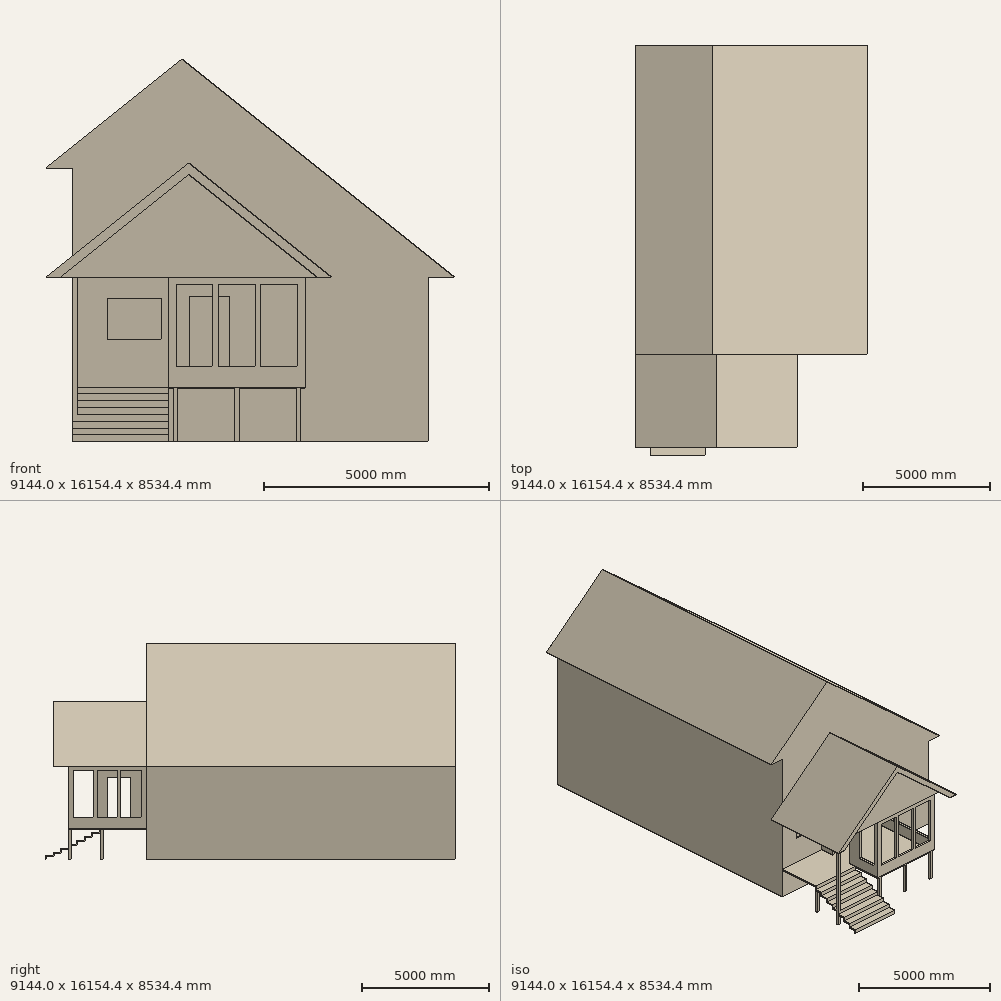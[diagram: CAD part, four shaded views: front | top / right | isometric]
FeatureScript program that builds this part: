
annotation { "Feature Type Name" : "Feature", "Feature Type Description" : "" }
export const myFeature = defineFeature(function(context is Context, id is Id, definition is map)
    precondition{}
    {
        {
            var Q0;
            Q0=qCreatedBy(makeId("Front.planeOp"),FACE);
            var sketch = newSketch(context, id + "F0", { "sketchPlane" : qUnion([Q0])});
            skLineSegment(sketch, "E0.bottom", {"start": v(0, 0) * mm, "end": v(-7924.8, 0) * mm});
            skLineSegment(sketch, "E1", {"start": v(-8534.4, 6096) * mm, "end": v(-7924.8, 6096) * mm});
            skLineSegment(sketch, "E2", {"start": v(0, 3657.6) * mm, "end": v(609.6, 3657.6) * mm});
            skLineSegment(sketch, "E3", {"start": v(-8534.4, 6096) * mm, "end": v(-5486.4, 8534.4) * mm});
            skLineSegment(sketch, "E4", {"start": v(0, 0) * mm, "end": v(0, 3657.6) * mm});
            skLineSegment(sketch, "E5", {"start": v(-7924.8, 0) * mm, "end": v(-7924.8, 6096) * mm});
            skLineSegment(sketch, "E6", {"start": v(-8534.4, 6096) * mm, "end": v(-2438.4, 6096) * mm, "construction": true});
            skLineSegment(sketch, "E7", {"start": v(-5486.4, 8534.4) * mm, "end": v(-2438.4, 6096) * mm});
            skLineSegment(sketch, "E8", {"start": v(-2438.4, 6096) * mm, "end": v(609.6, 3657.6) * mm});
            skSolve(sketch);
        }
        {
            var Q0;
            Q0=makeQuery(id+"F0.imprint","IMPRINT",FACE,{"disambiguationData":[TD([[makeQuery(id+"F0.imprint","IMPRINT",EDGE,{"derivedFrom":sQuery(id+"F0.wireOp",EDGE,"E0.bottom")}),-1.0]])]});
            extrude(context, id + "F1", {"entities" : qUnion([Q0]), "depth" : 12192 * mm, "offsetDistance" : 30.48 * mm});
        }
        {
            var Q0;
            Q0=makeQuery(id+"F1.opExtrude","CAP_FACE",FACE,{"disambiguationData":[OSD([sQuery(id+"F0.wireOp",EDGE,"E0.bottom"),sQuery(id+"F0.wireOp",EDGE,"E1"),sQuery(id+"F0.wireOp",EDGE,"E2"),sQuery(id+"F0.wireOp",EDGE,"E3"),sQuery(id+"F0.wireOp",EDGE,"IzW1YhJm-Oqc0-RvsV-s3cz-nyWO0slT3fW2"),sQuery(id+"F0.wireOp",EDGE,"E4"),sQuery(id+"F0.wireOp",EDGE,"E5")])],"isStart":false});
            var sketch = newSketch(context, id + "F2", { "sketchPlane" : qUnion([Q0])});
            skLineSegment(sketch, "E9", {"start": v(-7924.8, 1219.2) * mm, "end": v(0, 1219.2) * mm, "construction": true});
            skLineSegment(sketch, "E10.bottom", {"start": v(-7162.8, 3200.4) * mm, "end": v(-5943.6, 3200.4) * mm});
            skLineSegment(sketch, "E10.top", {"start": v(-7162.8, 2286) * mm, "end": v(-5943.6, 2286) * mm});
            skLineSegment(sketch, "E10.left", {"start": v(-7162.8, 3200.4) * mm, "end": v(-7162.8, 2286) * mm});
            skLineSegment(sketch, "E10.right", {"start": v(-5943.6, 3200.4) * mm, "end": v(-5943.6, 2286) * mm});
            skLineSegment(sketch, "E11.bottom", {"start": v(-5334, 1219.2) * mm, "end": v(-4419.6, 1219.2) * mm});
            skLineSegment(sketch, "E11.top", {"start": v(-5334, 3251.2) * mm, "end": v(-4419.6, 3251.2) * mm});
            skLineSegment(sketch, "E11.left", {"start": v(-5334, 1219.2) * mm, "end": v(-5334, 3251.2) * mm});
            skLineSegment(sketch, "E11.right", {"start": v(-4419.6, 1219.2) * mm, "end": v(-4419.6, 3251.2) * mm});
            skLineSegment(sketch, "E12", {"start": v(-8534.4, 3657.6) * mm, "end": v(-5334, 6217.92) * mm});
            skLineSegment(sketch, "E13", {"start": v(-5334, 6217.92) * mm, "end": v(-2133.6, 3657.6) * mm});
            skLineSegment(sketch, "E14", {"start": v(-2133.6, 3657.6) * mm, "end": v(-8534.4, 3657.6) * mm});
            skLineSegment(sketch, "E15.0", {"start": v(-5334, 5957.7) * mm, "end": v(-2712.88, 3860.8) * mm});
            skLineSegment(sketch, "E15.1", {"start": v(-7955.12, 3860.8) * mm, "end": v(-5334, 5957.7) * mm});
            skLineSegment(sketch, "E15.2", {"start": v(-2712.88, 3860.8) * mm, "end": v(-7955.12, 3860.8) * mm});
            skLineSegment(sketch, "E16", {"start": v(-7955.12, 3860.8) * mm, "end": v(-8209.12, 3657.6) * mm});
            skLineSegment(sketch, "E17", {"start": v(-2712.88, 3860.8) * mm, "end": v(-2458.88, 3657.6) * mm});
            skSolve(sketch);
        }
        {
            var Q0;
            Q0=makeQuery(id+"F1.opExtrude","SWEPT_FACE",FACE,{"disambiguationData":[OSD([sQuery(id+"F0.wireOp",EDGE,"E5")])]});
            var sketch = newSketch(context, id + "F3", { "sketchPlane" : qUnion([Q0])});
            skLineSegment(sketch, "E18", {"start": v(14020.8, 1219.2) * mm, "end": v(14020.8, 1066.8) * mm});
            skLineSegment(sketch, "E19", {"start": v(14020.8, 1066.8) * mm, "end": v(14325.6, 1066.8) * mm});
            skLineSegment(sketch, "E20", {"start": v(14325.6, 1066.8) * mm, "end": v(14325.6, 914.4) * mm});
            skLineSegment(sketch, "E21", {"start": v(14325.6, 914.4) * mm, "end": v(14630.4, 914.4) * mm});
            skLineSegment(sketch, "E22", {"start": v(14630.4, 914.4) * mm, "end": v(14630.4, 762) * mm});
            skLineSegment(sketch, "E23", {"start": v(14630.4, 762) * mm, "end": v(14935.2, 762) * mm});
            skLineSegment(sketch, "E24", {"start": v(14935.2, 762) * mm, "end": v(14935.2, 609.6) * mm});
            skLineSegment(sketch, "E25", {"start": v(14935.2, 609.6) * mm, "end": v(15240, 609.6) * mm});
            skLineSegment(sketch, "E26", {"start": v(15240, 609.6) * mm, "end": v(15240, 457.2) * mm});
            skLineSegment(sketch, "E27", {"start": v(15240, 457.2) * mm, "end": v(15544.8, 457.2) * mm});
            skLineSegment(sketch, "E28", {"start": v(15544.8, 457.2) * mm, "end": v(15544.8, 304.8) * mm});
            skLineSegment(sketch, "E29", {"start": v(15544.8, 304.8) * mm, "end": v(15849.6, 304.8) * mm});
            skLineSegment(sketch, "E30", {"start": v(15849.6, 304.8) * mm, "end": v(15849.6, 152.4) * mm});
            skLineSegment(sketch, "E31", {"start": v(15849.6, 152.4) * mm, "end": v(16154.4, 152.4) * mm});
            skLineSegment(sketch, "E32", {"start": v(16154.4, 152.4) * mm, "end": v(16154.4, 0) * mm});
            skLineSegment(sketch, "E33", {"start": v(14020.8, 1219.2) * mm, "end": v(12192, 1219.2) * mm});
            skLineSegment(sketch, "E34", {"start": v(16154.4, 0) * mm, "end": v(12192, 0) * mm});
            skLineSegment(sketch, "E35.0", {"start": v(13982.7, 1181.1) * mm, "end": v(12192, 1181.1) * mm});
            skLineSegment(sketch, "E35.1", {"start": v(13982.7, 1181.1) * mm, "end": v(13982.7, 1028.7) * mm});
            skLineSegment(sketch, "E35.2", {"start": v(13982.7, 1028.7) * mm, "end": v(14287.5, 1028.7) * mm});
            skLineSegment(sketch, "E35.3", {"start": v(14287.5, 1028.7) * mm, "end": v(14287.5, 876.3) * mm});
            skLineSegment(sketch, "E35.4", {"start": v(14287.5, 876.3) * mm, "end": v(14592.3, 876.3) * mm});
            skLineSegment(sketch, "E35.5", {"start": v(14592.3, 876.3) * mm, "end": v(14592.3, 723.9) * mm});
            skLineSegment(sketch, "E35.6", {"start": v(15506.7, 266.7) * mm, "end": v(15811.5, 266.7) * mm});
            skLineSegment(sketch, "E35.7", {"start": v(15811.5, 266.7) * mm, "end": v(15811.5, 114.3) * mm});
            skLineSegment(sketch, "E35.8", {"start": v(15811.5, 114.3) * mm, "end": v(16116.3, 114.3) * mm});
            skLineSegment(sketch, "E35.9", {"start": v(16116.3, 114.3) * mm, "end": v(16116.3, 0) * mm});
            skLineSegment(sketch, "E35.10", {"start": v(15506.7, 419.1) * mm, "end": v(15506.7, 266.7) * mm});
            skLineSegment(sketch, "E35.11", {"start": v(15201.9, 419.1) * mm, "end": v(15506.7, 419.1) * mm});
            skLineSegment(sketch, "E35.12", {"start": v(15201.9, 571.5) * mm, "end": v(15201.9, 419.1) * mm});
            skLineSegment(sketch, "E35.13", {"start": v(14897.1, 571.5) * mm, "end": v(15201.9, 571.5) * mm});
            skLineSegment(sketch, "E35.14", {"start": v(14897.1, 723.9) * mm, "end": v(14897.1, 571.5) * mm});
            skLineSegment(sketch, "E35.15", {"start": v(14592.3, 723.9) * mm, "end": v(14897.1, 723.9) * mm});
            skSolve(sketch);
        }
        {
            var Q0;
            Q0=makeQuery(id+"F3.imprint","IMPRINT",FACE,{"disambiguationData":[TD([[makeQuery(id+"F3.imprint","IMPRINT",EDGE,{"derivedFrom":sQuery(id+"F3.wireOp",EDGE,"E18")}),-1.0]])]});
            extrude(context, id + "F4", {"entities" : qUnion([Q0]), "oppositeDirection" : true, "depth" : 2133.6 * mm, "offsetDistance" : 30.48 * mm});
        }
        {
            var Q0;
            Q0=makeQuery(id+"F2.imprint","IMPRINT",FACE,{"disambiguationData":[TD([[makeQuery(id+"F2.imprint","IMPRINT",EDGE,{"derivedFrom":sQuery(id+"F2.wireOp",EDGE,"E10.bottom")}),-1.0]])]});
            var Q1;
            Q1=makeQuery(id+"F2.imprint","IMPRINT",FACE,{"disambiguationData":[TD([[makeQuery(id+"F2.imprint","IMPRINT",EDGE,{"derivedFrom":sQuery(id+"F2.wireOp",EDGE,"E11.bottom")}),1.0]])]});
            var Q2;
            {var subQ0=sQuery(id+"F2.wireOp",EDGE,"E14");var subQ1=sQuery(id+"F2.wireOp",EDGE,"E12");var subQ2=makeQuery(id+"F2.imprint","INTERSECT",VERTEX,{"derivedFrom":[subQ1,subQ0]});Q2=makeQuery(id+"F2.imprint","IMPRINT",FACE,{"disambiguationData":[TD([[makeQuery(id+"F2.imprint","IMPRINT",EDGE,{"disambiguationData":[TD([[subQ2,-1.0]])],"derivedFrom":subQ1}),-1.0]])]});}
            extrude(context, id + "F5", {"entities" : qUnion([Q0, Q1, Q2]), "operationType" : NewBodyOperationType.REMOVE, "oppositeDirection" : true, "depth" : 30.48 * mm, "offsetDistance" : 30.48 * mm});
        }
        {
            var Q0;
            Q0=makeQuery(id+"F4.opExtrude","CAP_FACE",FACE,{"disambiguationData":[OSD([sQuery(id+"F0.wireOp",EDGE,"E5"),sQuery(id+"F3.wireOp",EDGE,"E18"),sQuery(id+"F3.wireOp",EDGE,"E19"),sQuery(id+"F3.wireOp",EDGE,"E20"),sQuery(id+"F3.wireOp",EDGE,"E21"),sQuery(id+"F3.wireOp",EDGE,"E22"),sQuery(id+"F3.wireOp",EDGE,"E23"),sQuery(id+"F3.wireOp",EDGE,"E24"),sQuery(id+"F3.wireOp",EDGE,"E25"),sQuery(id+"F3.wireOp",EDGE,"E26"),sQuery(id+"F3.wireOp",EDGE,"E27"),sQuery(id+"F3.wireOp",EDGE,"E28"),sQuery(id+"F3.wireOp",EDGE,"E29"),sQuery(id+"F3.wireOp",EDGE,"E30"),sQuery(id+"F3.wireOp",EDGE,"E31"),sQuery(id+"F3.wireOp",EDGE,"E32"),sQuery(id+"F3.wireOp",EDGE,"E33"),sQuery(id+"F3.wireOp",EDGE,"E34")])],"isStart":false});
            var sketch = newSketch(context, id + "F6", { "sketchPlane" : qUnion([Q0])});
            skLineSegment(sketch, "E36", {"start": v(-12192, 1219.2) * mm, "end": v(-15240, 1219.2) * mm});
            skLineSegment(sketch, "E37", {"start": v(-15240, 1219.2) * mm, "end": v(-15240, 1181.1) * mm});
            skLineSegment(sketch, "E38", {"start": v(-15240, 1181.1) * mm, "end": v(-12192, 1181.1) * mm});
            skLineSegment(sketch, "E39", {"start": v(-12192, 1181.1) * mm, "end": v(-12192, 1219.2) * mm});
            skSolve(sketch);
        }
        {
            var Q0;
            {var subQ3=sQuery(id+"F6.wireOp",EDGE,"E37");Q0=makeQuery(id+"F6.imprint","IMPRINT",FACE,{"disambiguationData":[TD([[makeQuery(id+"F6.imprint","IMPRINT",EDGE,{"derivedFrom":subQ3}),1.0]])]});}
            var Q1;
            {var subQ3=sQuery(id+"F6.wireOp",EDGE,"E39");Q1=makeQuery(id+"F6.imprint","IMPRINT",FACE,{"disambiguationData":[TD([[makeQuery(id+"F6.imprint","IMPRINT",EDGE,{"derivedFrom":subQ3}),1.0]])]});}
            extrude(context, id + "F7", {"entities" : qUnion([Q0, Q1]), "depth" : 3048 * mm, "offsetDistance" : 30.48 * mm});
        }
        {
            var Q0;
            Q0=makeQuery(id+"F7.opExtrude","SWEPT_FACE",FACE,{"disambiguationData":[OSD([sQuery(id+"F6.wireOp",EDGE,"E38")])]});
            var sketch = newSketch(context, id + "F8", { "sketchPlane" : qUnion([Q0])});
            skLineSegment(sketch, "E40.bottom", {"start": v(-5689.6, 15240) * mm, "end": v(-5588, 15240) * mm});
            skLineSegment(sketch, "E40.top", {"start": v(-5689.6, 15138.4) * mm, "end": v(-5588, 15138.4) * mm});
            skLineSegment(sketch, "E40.left", {"start": v(-5689.6, 15240) * mm, "end": v(-5689.6, 15138.4) * mm});
            skLineSegment(sketch, "E40.right", {"start": v(-5588, 15240) * mm, "end": v(-5588, 15138.4) * mm});
            skLineSegment(sketch, "E41.bottom", {"start": v(-2844.8, 15240) * mm, "end": v(-2946.4, 15240) * mm});
            skLineSegment(sketch, "E41.top", {"start": v(-2844.8, 15138.4) * mm, "end": v(-2946.4, 15138.4) * mm});
            skLineSegment(sketch, "E41.left", {"start": v(-2844.8, 15240) * mm, "end": v(-2844.8, 15138.4) * mm});
            skLineSegment(sketch, "E41.right", {"start": v(-2946.4, 15240) * mm, "end": v(-2946.4, 15138.4) * mm});
            skLineSegment(sketch, "E42.bottom", {"start": v(-4216.4, 15240) * mm, "end": v(-4318, 15240) * mm});
            skLineSegment(sketch, "E42.top", {"start": v(-4216.4, 15138.4) * mm, "end": v(-4318, 15138.4) * mm});
            skLineSegment(sketch, "E42.left", {"start": v(-4216.4, 15240) * mm, "end": v(-4216.4, 15138.4) * mm});
            skLineSegment(sketch, "E42.right", {"start": v(-4318, 15240) * mm, "end": v(-4318, 15138.4) * mm});
            skLineSegment(sketch, "E43.bottom", {"start": v(-7823.2, 13982.7) * mm, "end": v(-7721.6, 13982.7) * mm});
            skLineSegment(sketch, "E43.top", {"start": v(-7823.2, 13881.1) * mm, "end": v(-7721.6, 13881.1) * mm});
            skLineSegment(sketch, "E43.left", {"start": v(-7823.2, 13982.7) * mm, "end": v(-7823.2, 13881.1) * mm});
            skLineSegment(sketch, "E43.right", {"start": v(-7721.6, 13982.7) * mm, "end": v(-7721.6, 13881.1) * mm});
            skLineSegment(sketch, "E44.bottom", {"start": v(-5994.4, 13881.1) * mm, "end": v(-5892.8, 13881.1) * mm});
            skLineSegment(sketch, "E44.top", {"start": v(-5994.4, 13982.7) * mm, "end": v(-5892.8, 13982.7) * mm});
            skLineSegment(sketch, "E44.left", {"start": v(-5994.4, 13881.1) * mm, "end": v(-5994.4, 13982.7) * mm});
            skLineSegment(sketch, "E44.right", {"start": v(-5892.8, 13881.1) * mm, "end": v(-5892.8, 13982.7) * mm});
            skSolve(sketch);
        }
        {
            var Q0;
            Q0=makeQuery(id+"F8.imprint","IMPRINT",FACE,{"disambiguationData":[TD([[makeQuery(id+"F8.imprint","IMPRINT",EDGE,{"derivedFrom":sQuery(id+"F8.wireOp",EDGE,"E44.bottom")}),1.0]])]});
            var Q1;
            Q1=makeQuery(id+"F8.imprint","IMPRINT",FACE,{"disambiguationData":[TD([[makeQuery(id+"F8.imprint","IMPRINT",EDGE,{"derivedFrom":sQuery(id+"F8.wireOp",EDGE,"E40.bottom")}),-1.0]])]});
            var Q2;
            Q2=makeQuery(id+"F8.imprint","IMPRINT",FACE,{"disambiguationData":[TD([[makeQuery(id+"F8.imprint","IMPRINT",EDGE,{"derivedFrom":sQuery(id+"F8.wireOp",EDGE,"E42.bottom")}),1.0]])]});
            var Q3;
            Q3=makeQuery(id+"F8.imprint","IMPRINT",FACE,{"disambiguationData":[TD([[makeQuery(id+"F8.imprint","IMPRINT",EDGE,{"derivedFrom":sQuery(id+"F8.wireOp",EDGE,"E41.bottom")}),1.0]])]});
            var Q4;
            Q4=makeQuery(id+"F8.imprint","IMPRINT",FACE,{"disambiguationData":[TD([[makeQuery(id+"F8.imprint","IMPRINT",EDGE,{"derivedFrom":sQuery(id+"F8.wireOp",EDGE,"E43.bottom")}),-1.0]])]});
            var Q5;
            Q5=makeQuery(id+"F8.imprint","IMPRINT",FACE,{"disambiguationData":[TD([[makeQuery(id+"F8.imprint","IMPRINT",EDGE,{"derivedFrom":sQuery(id+"F8.wireOp",EDGE,"E40.bottom")}),1.0]])]});
            extrude(context, id + "F9", {"entities" : qUnion([Q0, Q1, Q2, Q3, Q4, Q5]), "depth" : 1181.1 * mm, "offsetDistance" : 30.48 * mm});
        }
        {
            var Q0;
            Q0=makeQuery(id+"F9.opExtrude","SWEPT_BODY",BODY,{"disambiguationData":[OSD([sQuery(id+"F8.wireOp",EDGE,"E41.bottom"),sQuery(id+"F8.wireOp",EDGE,"E41.top"),sQuery(id+"F8.wireOp",EDGE,"E41.left"),sQuery(id+"F8.wireOp",EDGE,"E41.right")])]});
            var Q1;
            Q1=makeQuery(id+"F9.opExtrude","SWEPT_BODY",BODY,{"disambiguationData":[OSD([sQuery(id+"F8.wireOp",EDGE,"E40.bottom"),sQuery(id+"F8.wireOp",EDGE,"E40.top"),sQuery(id+"F8.wireOp",EDGE,"E40.left"),sQuery(id+"F8.wireOp",EDGE,"E40.right")])]});
            var Q2;
            Q2=makeQuery(id+"F7.opExtrude","SWEPT_BODY",BODY,{"disambiguationData":[OSD([sQuery(id+"F6.wireOp",EDGE,"E36"),sQuery(id+"F6.wireOp",EDGE,"E37"),sQuery(id+"F6.wireOp",EDGE,"E38"),sQuery(id+"F6.wireOp",EDGE,"E39")])]});
            var Q3;
            Q3=makeQuery(id+"F4.opExtrude","SWEPT_BODY",BODY,{"disambiguationData":[OSD([sQuery(id+"F0.wireOp",EDGE,"E5"),sQuery(id+"F3.wireOp",EDGE,"E18"),sQuery(id+"F3.wireOp",EDGE,"E19"),sQuery(id+"F3.wireOp",EDGE,"E20"),sQuery(id+"F3.wireOp",EDGE,"E21"),sQuery(id+"F3.wireOp",EDGE,"E22"),sQuery(id+"F3.wireOp",EDGE,"E23"),sQuery(id+"F3.wireOp",EDGE,"E24"),sQuery(id+"F3.wireOp",EDGE,"E25"),sQuery(id+"F3.wireOp",EDGE,"E26"),sQuery(id+"F3.wireOp",EDGE,"E27"),sQuery(id+"F3.wireOp",EDGE,"E28"),sQuery(id+"F3.wireOp",EDGE,"E29"),sQuery(id+"F3.wireOp",EDGE,"E30"),sQuery(id+"F3.wireOp",EDGE,"E31"),sQuery(id+"F3.wireOp",EDGE,"E32"),sQuery(id+"F3.wireOp",EDGE,"E33"),sQuery(id+"F3.wireOp",EDGE,"E34"),sQuery(id+"F3.wireOp",EDGE,"E35.0"),sQuery(id+"F3.wireOp",EDGE,"E35.1"),sQuery(id+"F3.wireOp",EDGE,"E35.2"),sQuery(id+"F3.wireOp",EDGE,"E35.3"),sQuery(id+"F3.wireOp",EDGE,"E35.4"),sQuery(id+"F3.wireOp",EDGE,"E35.5"),sQuery(id+"F3.wireOp",EDGE,"E35.6"),sQuery(id+"F3.wireOp",EDGE,"E35.7"),sQuery(id+"F3.wireOp",EDGE,"E35.8"),sQuery(id+"F3.wireOp",EDGE,"E35.9"),sQuery(id+"F3.wireOp",EDGE,"E35.10"),sQuery(id+"F3.wireOp",EDGE,"E35.11"),sQuery(id+"F3.wireOp",EDGE,"E35.12"),sQuery(id+"F3.wireOp",EDGE,"E35.13"),sQuery(id+"F3.wireOp",EDGE,"E35.14"),sQuery(id+"F3.wireOp",EDGE,"E35.15")])]});
            var Q4;
            Q4=makeQuery(id+"F9.opExtrude","SWEPT_BODY",BODY,{"disambiguationData":[OSD([sQuery(id+"F8.wireOp",EDGE,"E44.bottom"),sQuery(id+"F8.wireOp",EDGE,"E44.top"),sQuery(id+"F8.wireOp",EDGE,"E44.left"),sQuery(id+"F8.wireOp",EDGE,"E44.right")])]});
            var Q5;
            Q5=makeQuery(id+"F9.opExtrude","SWEPT_BODY",BODY,{"disambiguationData":[OSD([sQuery(id+"F8.wireOp",EDGE,"E43.bottom"),sQuery(id+"F8.wireOp",EDGE,"E43.top"),sQuery(id+"F8.wireOp",EDGE,"E43.left"),sQuery(id+"F8.wireOp",EDGE,"E43.right")])]});
            var Q6;
            Q6=makeQuery(id+"F9.opExtrude","SWEPT_BODY",BODY,{"disambiguationData":[OSD([sQuery(id+"F8.wireOp",EDGE,"E42.bottom"),sQuery(id+"F8.wireOp",EDGE,"E42.top"),sQuery(id+"F8.wireOp",EDGE,"E42.left"),sQuery(id+"F8.wireOp",EDGE,"E42.right")])]});
            booleanBodies(context, id + "F10", {"operationType" : BooleanOperationType.UNION, "tools" : qUnion([Q0, Q1, Q2, Q3, Q4, Q5, Q6])});
        }
        {
            var Q0;
            Q0=makeQuery(id+"F10.opBoolean","MERGE",FACE,{"derivedFrom":[makeQuery(id+"F4.opExtrude","SWEPT_FACE",FACE,{"disambiguationData":[OSD([sQuery(id+"F3.wireOp",EDGE,"E33")])]}),makeQuery(id+"F7.opExtrude","SWEPT_FACE",FACE,{"disambiguationData":[OSD([sQuery(id+"F6.wireOp",EDGE,"E36")])]})]});
            var sketch = newSketch(context, id + "F11", { "sketchPlane" : qUnion([Q0])});
            skLineSegment(sketch, "E45.bottom", {"start": v(-5791.2, -15240) * mm, "end": v(-2743.2, -15240) * mm});
            skLineSegment(sketch, "E45.top", {"start": v(-5791.2, -12192) * mm, "end": v(-2743.2, -12192) * mm});
            skLineSegment(sketch, "E45.left", {"start": v(-5791.2, -15240) * mm, "end": v(-5791.2, -12192) * mm});
            skLineSegment(sketch, "E45.right", {"start": v(-2743.2, -15240) * mm, "end": v(-2743.2, -12192) * mm});
            skLineSegment(sketch, "E46.top", {"start": v(-2844.8, -15138.4) * mm, "end": v(-5689.6, -15138.4) * mm});
            skLineSegment(sketch, "E46.left", {"start": v(-2844.8, -12192) * mm, "end": v(-2844.8, -15138.4) * mm});
            skLineSegment(sketch, "E46.right", {"start": v(-5689.6, -12192) * mm, "end": v(-5689.6, -15138.4) * mm});
            skSolve(sketch);
        }
        {
            var Q0;
            {var subQ8=sQuery(id+"F11.wireOp",EDGE,"E45.bottom");Q0=makeQuery(id+"F11.imprint","IMPRINT",FACE,{"disambiguationData":[TD([[makeQuery(id+"F11.imprint","IMPRINT",EDGE,{"derivedFrom":subQ8}),-1.0]])]});}
            extrude(context, id + "F12", {"entities" : qUnion([Q0]), "depth" : 2438.4 * mm, "offsetDistance" : 30.48 * mm});
        }
        {
            var Q0;
            Q0=makeQuery(id+"F4.opExtrude","SWEPT_FACE",FACE,{"disambiguationData":[OSD([sQuery(id+"F3.wireOp",EDGE,"E25")])]});
            var sketch = newSketch(context, id + "F13", { "sketchPlane" : qUnion([Q0])});
            skLineSegment(sketch, "E47.bottom", {"start": v(-7924.8, -15240) * mm, "end": v(-7823.2, -15240) * mm});
            skLineSegment(sketch, "E47.top", {"start": v(-7924.8, -15138.4) * mm, "end": v(-7823.2, -15138.4) * mm});
            skLineSegment(sketch, "E47.left", {"start": v(-7924.8, -15240) * mm, "end": v(-7924.8, -15138.4) * mm});
            skLineSegment(sketch, "E47.right", {"start": v(-7823.2, -15240) * mm, "end": v(-7823.2, -15138.4) * mm});
            skSolve(sketch);
        }
        {
            var Q0;
            Q0=qSketchRegion(id+"F13",true);
            extrude(context, id + "F14", {"entities" : qUnion([Q0]), "operationType" : NewBodyOperationType.ADD, "depth" : 3048 * mm, "offsetDistance" : 30.48 * mm});
        }
        {
            var Q0;
            Q0=makeQuery(id+"F12.opExtrude","SWEPT_FACE",FACE,{"disambiguationData":[OSD([sQuery(id+"F11.wireOp",EDGE,"E45.bottom")])]});
            var sketch = newSketch(context, id + "F15", { "sketchPlane" : qUnion([Q0])});
            skLineSegment(sketch, "E48.bottom", {"start": v(-5613.4, 3505.2) * mm, "end": v(-4800.6, 3505.2) * mm});
            skLineSegment(sketch, "E48.top", {"start": v(-5613.4, 1676.4) * mm, "end": v(-4800.6, 1676.4) * mm});
            skLineSegment(sketch, "E48.left", {"start": v(-5613.4, 3505.2) * mm, "end": v(-5613.4, 1676.4) * mm});
            skLineSegment(sketch, "E48.right", {"start": v(-4800.6, 3505.2) * mm, "end": v(-4800.6, 1676.4) * mm});
            skLineSegment(sketch, "E49.bottom", {"start": v(-4673.6, 1676.4) * mm, "end": v(-3860.8, 1676.4) * mm});
            skLineSegment(sketch, "E49.top", {"start": v(-4673.6, 3505.2) * mm, "end": v(-3860.8, 3505.2) * mm});
            skLineSegment(sketch, "E49.left", {"start": v(-4673.6, 1676.4) * mm, "end": v(-4673.6, 3505.2) * mm});
            skLineSegment(sketch, "E49.right", {"start": v(-3860.8, 1676.4) * mm, "end": v(-3860.8, 3505.2) * mm});
            skLineSegment(sketch, "E50.bottom", {"start": v(-3733.8, 3505.2) * mm, "end": v(-2921, 3505.2) * mm});
            skLineSegment(sketch, "E50.top", {"start": v(-3733.8, 1676.4) * mm, "end": v(-2921, 1676.4) * mm});
            skLineSegment(sketch, "E50.left", {"start": v(-3733.8, 3505.2) * mm, "end": v(-3733.8, 1676.4) * mm});
            skLineSegment(sketch, "E50.right", {"start": v(-2921, 3505.2) * mm, "end": v(-2921, 1676.4) * mm});
            skSolve(sketch);
        }
        {
            var Q0;
            Q0=qSketchRegion(id+"F15",true);
            extrude(context, id + "F16", {"entities" : qUnion([Q0]), "operationType" : NewBodyOperationType.REMOVE, "oppositeDirection" : true, "depth" : 304.8 * mm, "offsetDistance" : 30.48 * mm});
        }
        {
            var Q0;
            Q0=makeQuery(id+"F12.opExtrude","SWEPT_FACE",FACE,{"disambiguationData":[OSD([sQuery(id+"F11.wireOp",EDGE,"E45.right")])]});
            var sketch = newSketch(context, id + "F17", { "sketchPlane" : qUnion([Q0])});
            skLineSegment(sketch, "E51.bottom", {"start": v(-15062.2, 3505.2) * mm, "end": v(-14249.4, 3505.2) * mm});
            skLineSegment(sketch, "E51.top", {"start": v(-15062.2, 1676.4) * mm, "end": v(-14249.4, 1676.4) * mm});
            skLineSegment(sketch, "E51.left", {"start": v(-15062.2, 3505.2) * mm, "end": v(-15062.2, 1676.4) * mm});
            skLineSegment(sketch, "E51.right", {"start": v(-14249.4, 3505.2) * mm, "end": v(-14249.4, 1676.4) * mm});
            skLineSegment(sketch, "E52.bottom", {"start": v(-14122.4, 1676.4) * mm, "end": v(-13309.6, 1676.4) * mm});
            skLineSegment(sketch, "E52.top", {"start": v(-14122.4, 3505.2) * mm, "end": v(-13309.6, 3505.2) * mm});
            skLineSegment(sketch, "E52.left", {"start": v(-14122.4, 1676.4) * mm, "end": v(-14122.4, 3505.2) * mm});
            skLineSegment(sketch, "E52.right", {"start": v(-13309.6, 1676.4) * mm, "end": v(-13309.6, 3505.2) * mm});
            skLineSegment(sketch, "E53.bottom", {"start": v(-13182.6, 3505.2) * mm, "end": v(-12369.8, 3505.2) * mm});
            skLineSegment(sketch, "E53.top", {"start": v(-13182.6, 1676.4) * mm, "end": v(-12369.8, 1676.4) * mm});
            skLineSegment(sketch, "E53.left", {"start": v(-13182.6, 3505.2) * mm, "end": v(-13182.6, 1676.4) * mm});
            skLineSegment(sketch, "E53.right", {"start": v(-12369.8, 3505.2) * mm, "end": v(-12369.8, 1676.4) * mm});
            skSolve(sketch);
        }
        {
            var Q0;
            Q0=qSketchRegion(id+"F17",true);
            extrude(context, id + "F18", {"entities" : qUnion([Q0]), "operationType" : NewBodyOperationType.REMOVE, "oppositeDirection" : true, "depth" : 304.8 * mm, "offsetDistance" : 30.48 * mm});
        }
        {
            var Q0;
            Q0=makeQuery(id+"F12.opExtrude","SWEPT_FACE",FACE,{"disambiguationData":[OSD([sQuery(id+"F11.wireOp",EDGE,"E45.left")])]});
            var sketch = newSketch(context, id + "F19", { "sketchPlane" : qUnion([Q0])});
            skLineSegment(sketch, "E54.bottom", {"start": v(12801.6, 1219.2) * mm, "end": v(13716, 1219.2) * mm});
            skLineSegment(sketch, "E54.top", {"start": v(12801.6, 3251.2) * mm, "end": v(13716, 3251.2) * mm});
            skLineSegment(sketch, "E54.left", {"start": v(12801.6, 1219.2) * mm, "end": v(12801.6, 3251.2) * mm});
            skLineSegment(sketch, "E54.right", {"start": v(13716, 1219.2) * mm, "end": v(13716, 3251.2) * mm});
            skLineSegment(sketch, "E55.bottom", {"start": v(14249.4, 3505.2) * mm, "end": v(15062.2, 3505.2) * mm});
            skLineSegment(sketch, "E55.top", {"start": v(14249.4, 1676.4) * mm, "end": v(15062.2, 1676.4) * mm});
            skLineSegment(sketch, "E55.left", {"start": v(14249.4, 3505.2) * mm, "end": v(14249.4, 1676.4) * mm});
            skLineSegment(sketch, "E55.right", {"start": v(15062.2, 3505.2) * mm, "end": v(15062.2, 1676.4) * mm});
            skSolve(sketch);
        }
        {
            var Q0;
            Q0=makeQuery(id+"F19.imprint","IMPRINT",FACE,{"disambiguationData":[TD([[makeQuery(id+"F19.imprint","IMPRINT",EDGE,{"derivedFrom":sQuery(id+"F19.wireOp",EDGE,"E54.bottom")}),-1.0]])]});
            var Q1;
            Q1=makeQuery(id+"F19.imprint","IMPRINT",FACE,{"disambiguationData":[TD([[makeQuery(id+"F19.imprint","IMPRINT",EDGE,{"derivedFrom":sQuery(id+"F19.wireOp",EDGE,"E55.bottom")}),-1.0]])]});
            extrude(context, id + "F20", {"entities" : qUnion([Q0, Q1]), "operationType" : NewBodyOperationType.REMOVE, "oppositeDirection" : true, "depth" : 304.8 * mm, "offsetDistance" : 30.48 * mm});
        }
        {
            var Q0;
            {var subQ0=sQuery(id+"F2.wireOp",EDGE,"E15.0");Q0=makeQuery(id+"F2.imprint","IMPRINT",FACE,{"disambiguationData":[TD([[makeQuery(id+"F2.imprint","IMPRINT",EDGE,{"derivedFrom":subQ0}),-1.0]])]});}
            var Q1;
            {var subQ0=sQuery(id+"F2.wireOp",EDGE,"E17");Q1=makeQuery(id+"F2.imprint","IMPRINT",FACE,{"disambiguationData":[TD([[makeQuery(id+"F2.imprint","IMPRINT",EDGE,{"derivedFrom":subQ0}),-1.0]])]});}
            var Q2;
            {var subQ0=sQuery(id+"F2.wireOp",EDGE,"E16");Q2=makeQuery(id+"F2.imprint","IMPRINT",FACE,{"disambiguationData":[TD([[makeQuery(id+"F2.imprint","IMPRINT",EDGE,{"derivedFrom":subQ0}),1.0]])]});}
            extrude(context, id + "F21", {"entities" : qUnion([Q0, Q1, Q2]), "depth" : 3048 * mm, "offsetDistance" : 30.48 * mm});
        }
        {
            var Q0;
            {var subQ1=sQuery(id+"F2.wireOp",EDGE,"E13");Q0=makeQuery(id+"F2.imprint","IMPRINT",FACE,{"disambiguationData":[TD([[makeQuery(id+"F2.imprint","IMPRINT",EDGE,{"derivedFrom":subQ1}),-1.0]])]});}
            var Q1;
            {var subQ0=sQuery(id+"F2.wireOp",EDGE,"E16");Q1=makeQuery(id+"F2.imprint","IMPRINT",FACE,{"disambiguationData":[TD([[makeQuery(id+"F2.imprint","IMPRINT",EDGE,{"derivedFrom":subQ0}),-1.0]])]});}
            extrude(context, id + "F22", {"entities" : qUnion([Q0, Q1]), "depth" : 3657.6 * mm, "offsetDistance" : 30.48 * mm});
        }
        {
            var Q0;
            Q0=makeQuery(id+"F13.imprint","IMPRINT",FACE,{"disambiguationData":[TD([[makeQuery(id+"F13.imprint","IMPRINT",EDGE,{"derivedFrom":sQuery(id+"F13.wireOp",EDGE,"E47.bottom")}),-1.0]])]});
            extrude(context, id + "F23", {"entities" : qUnion([Q0]), "operationType" : NewBodyOperationType.ADD, "oppositeDirection" : true, "depth" : 609.6 * mm, "offsetDistance" : 30.48 * mm});
        }
    });
